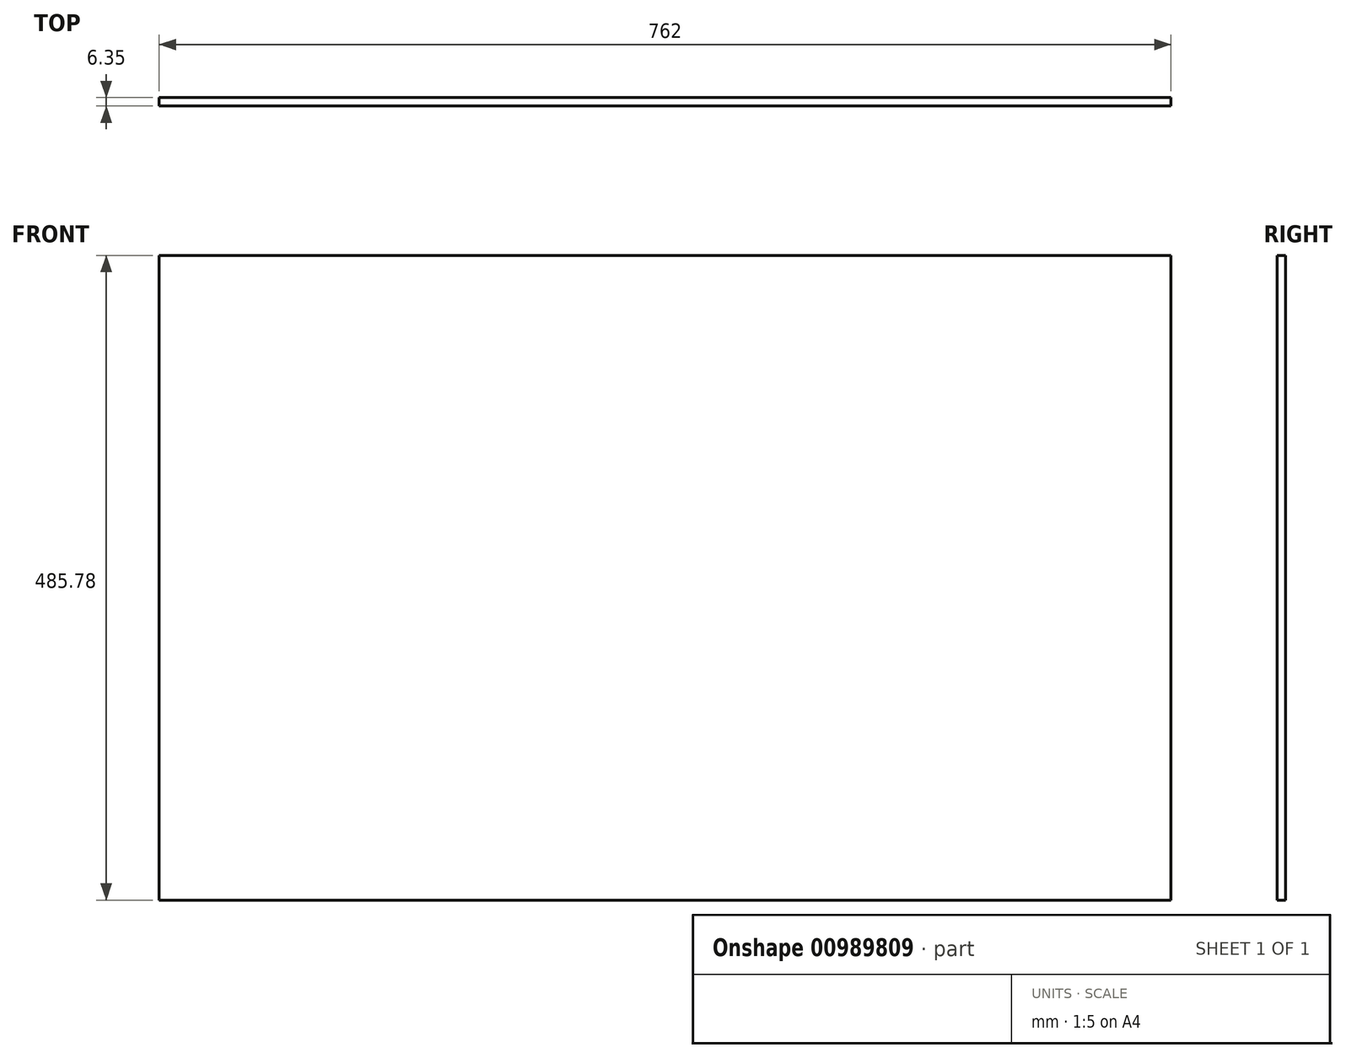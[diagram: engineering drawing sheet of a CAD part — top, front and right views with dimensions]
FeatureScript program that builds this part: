
annotation { "Feature Type Name" : "Feature", "Feature Type Description" : "" }
export const myFeature = defineFeature(function(context is Context, id is Id, definition is map)
    precondition{}
    {
        {
            var Q0;
            Q0=qCreatedBy(makeId("Front.planeOp"),FACE);
            var sketch = newSketch(context, id + "F0", { "sketchPlane" : qUnion([Q0])});
            skLineSegment(sketch, "E0.bottom", {"start": v(-381, 242.89) * mm, "end": v(381, 242.89) * mm});
            skLineSegment(sketch, "E0.top", {"start": v(-381, -242.89) * mm, "end": v(381, -242.89) * mm});
            skLineSegment(sketch, "E0.left", {"start": v(-381, 242.89) * mm, "end": v(-381, -242.89) * mm});
            skLineSegment(sketch, "E0.right", {"start": v(381, 242.89) * mm, "end": v(381, -242.89) * mm});
            skSolve(sketch);
        }
        {
            var Q0;
            Q0=makeQuery(id+"F0.imprint","IMPRINT",FACE,{"disambiguationData":[TD([[makeQuery(id+"F0.imprint","IMPRINT",EDGE,{"derivedFrom":sQuery(id+"F0.wireOp",EDGE,"E0.bottom")}),-1.0]])]});
            extrude(context, id + "F1", {"entities" : qUnion([Q0]), "depth" : 6.35 * mm, "offsetDistance" : 25.4 * mm});
        }
    });
